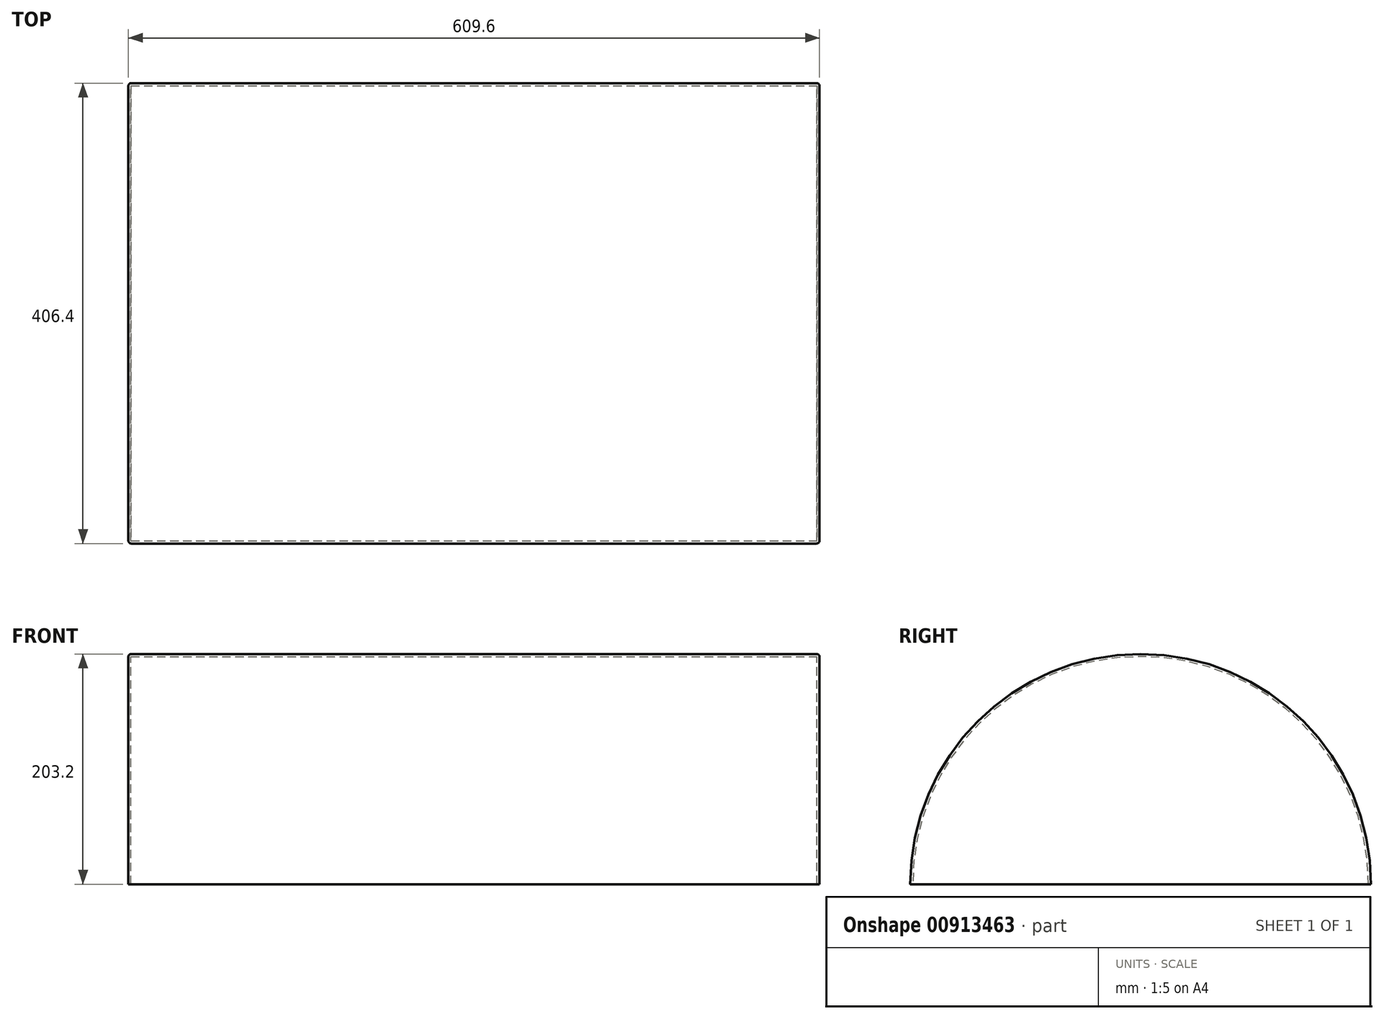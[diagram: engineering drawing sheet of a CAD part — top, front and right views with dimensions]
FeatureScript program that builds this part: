
annotation { "Feature Type Name" : "Feature", "Feature Type Description" : "" }
export const myFeature = defineFeature(function(context is Context, id is Id, definition is map)
    precondition{}
    {
        {
            var Q0;
            Q0=qCreatedBy(makeId("Front.planeOp"),FACE);
            var sketch = newSketch(context, id + "F0", { "sketchPlane" : qUnion([Q0])});
            skLineSegment(sketch, "E0.bottom", {"start": v(0, 0) * mm, "end": v(-609.6, 0) * mm});
            skLineSegment(sketch, "E0.top", {"start": v(0, -203.2) * mm, "end": v(-609.6, -203.2) * mm});
            skLineSegment(sketch, "E0.left", {"start": v(0, 0) * mm, "end": v(0, -203.2) * mm});
            skLineSegment(sketch, "E0.right", {"start": v(-609.6, 0) * mm, "end": v(-609.6, -203.2) * mm});
            skSolve(sketch);
        }
        {
            var Q0;
            Q0=makeQuery(id+"F0.imprint","IMPRINT",FACE,{"disambiguationData":[TD([[makeQuery(id+"F0.imprint","IMPRINT",EDGE,{"derivedFrom":sQuery(id+"F0.wireOp",EDGE,"E0.bottom")}),1.0]])]});
            extrude(context, id + "F1", {"entities" : qUnion([Q0]), "endBound" : BoundingType.SYMMETRIC, "depth" : 406.4 * mm, "offsetDistance" : 25.4 * mm});
        }
        {
            var Q0;
            Q0=makeQuery(id+"F1.opExtrude","CAP_EDGE",EDGE,{"disambiguationData":[OSD([sQuery(id+"F0.wireOp",EDGE,"E0.bottom")])],"isStart":false});
            var Q1;
            Q1=makeQuery(id+"F1.opExtrude","CAP_EDGE",EDGE,{"disambiguationData":[OSD([sQuery(id+"F0.wireOp",EDGE,"E0.bottom")])],"isStart":true});
            fillet(context, id + "F2", {"entities" : qUnion([Q0, Q1]), "radius" : 203.2 * mm, "tangentPropagation" : true, "allowEdgeOverflow" : false});
        }
        {
            var Q0;
            Q0=makeQuery(id+"F1.opExtrude","SWEPT_FACE",FACE,{"disambiguationData":[OSD([sQuery(id+"F0.wireOp",EDGE,"E0.top")])]});
            shell(context, id + "F3", {"entities" : qUnion([Q0]), "thickness" : 2.24 * mm});
        }
        {
            var Q0;
            Q0=makeQuery(id+"F2.opFillet","BLEND_EDGE",EDGE,{"blendedFrom":[makeQuery(id+"F1.opExtrude","CAP_EDGE",EDGE,{"disambiguationData":[OSD([sQuery(id+"F0.wireOp",EDGE,"E0.bottom")])],"isStart":true}),makeQuery(id+"F1.opExtrude","SWEPT_FACE",FACE,{"disambiguationData":[OSD([sQuery(id+"F0.wireOp",EDGE,"E0.left")])]})],"blendedInto":[makeQuery(id+"F1.opExtrude","SWEPT_FACE",FACE,{"disambiguationData":[OSD([sQuery(id+"F0.wireOp",EDGE,"E0.left")])]})]});
            var Q1;
            Q1=makeQuery(id+"F2.opFillet","BLEND_EDGE",EDGE,{"blendedFrom":[makeQuery(id+"F1.opExtrude","CAP_EDGE",EDGE,{"disambiguationData":[OSD([sQuery(id+"F0.wireOp",EDGE,"E0.bottom")])],"isStart":true}),makeQuery(id+"F1.opExtrude","SWEPT_FACE",FACE,{"disambiguationData":[OSD([sQuery(id+"F0.wireOp",EDGE,"E0.right")])]})],"blendedInto":[makeQuery(id+"F1.opExtrude","SWEPT_FACE",FACE,{"disambiguationData":[OSD([sQuery(id+"F0.wireOp",EDGE,"E0.right")])]})]});
            fillet(context, id + "F4", {"entities" : qUnion([Q0, Q1]), "radius" : 2.54 * mm, "tangentPropagation" : true, "allowEdgeOverflow" : false});
        }
    });
